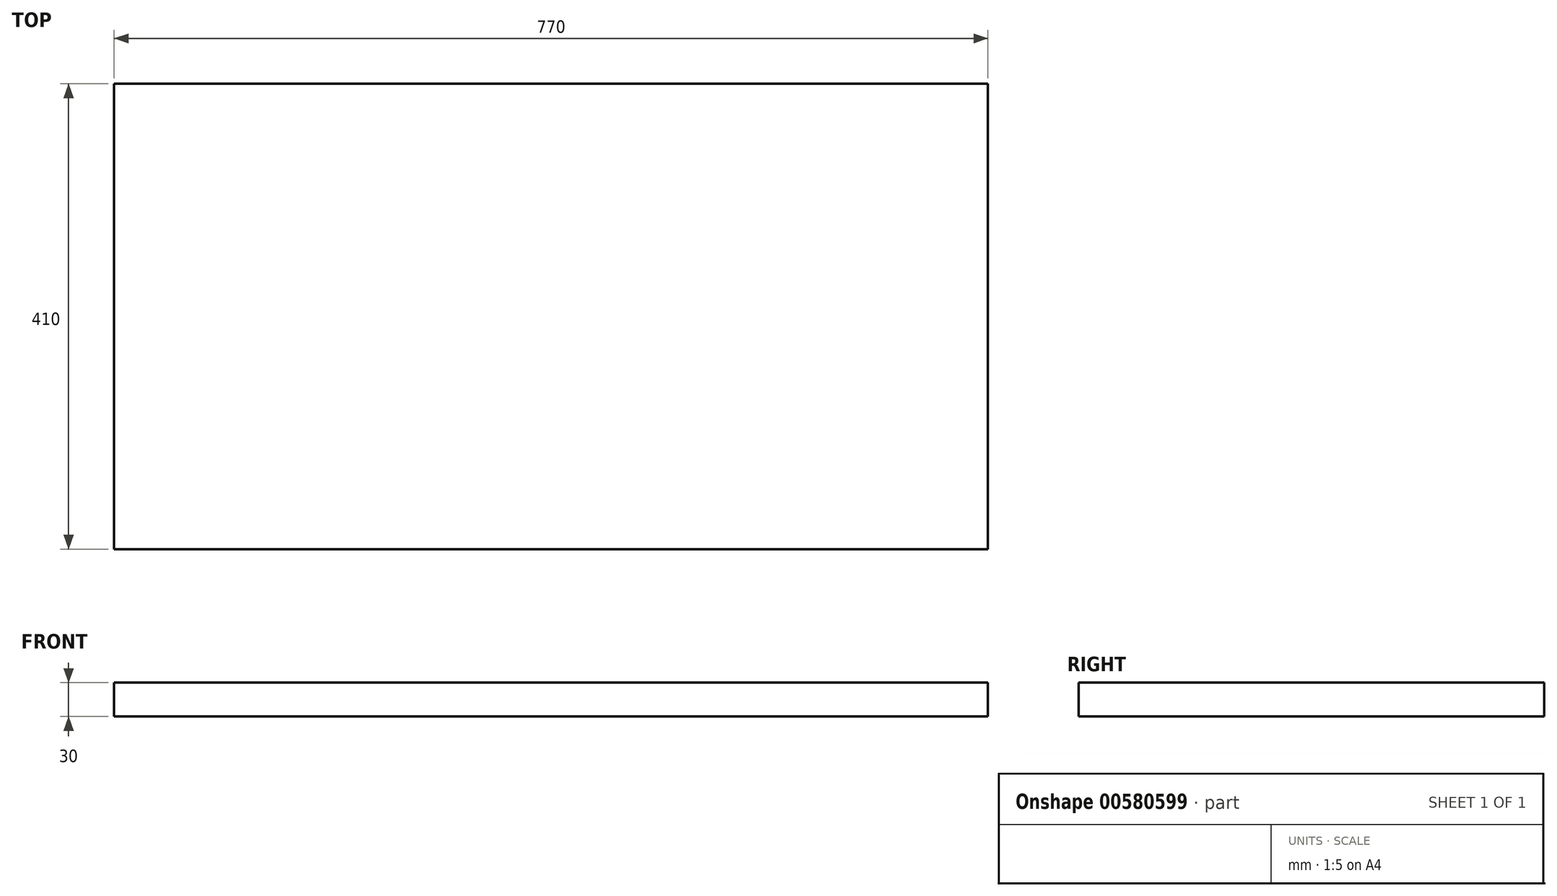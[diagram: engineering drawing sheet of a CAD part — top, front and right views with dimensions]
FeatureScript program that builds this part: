
annotation { "Feature Type Name" : "Feature", "Feature Type Description" : "" }
export const myFeature = defineFeature(function(context is Context, id is Id, definition is map)
    precondition{}
    {
        {
            var Q0;
            Q0=qCreatedBy(makeId("Top.planeOp"),FACE);
            var sketch = newSketch(context, id + "F0", { "sketchPlane" : qUnion([Q0])});
            skFitSpline(sketch, "E0", {"points": [v(0, 23.64) * mm, v(7.35, 24.1) * mm, v(20.44, 20.95) * mm, v(27.7, 15.75) * mm, v(39.9, 10.55) * mm, v(42.68, 9.83) * mm, v(45.82, 6.78) * mm, v(53.35, 1.76) * mm, v(55.77, -6.76) * mm, v(48.42, -21.1) * mm, v(34.34, -25.77) * mm, v(23.94, -26.85) * mm, v(14.7, -26.67) * mm, v(-6.73, -17.97) * mm, v(-18.48, -17.52) * mm, v(-30.68, -16.9) * mm, v(-37.94, -15.28) * mm, v(-41, -15.82) * mm, v(-49.6, -10.26) * mm, v(-55.7, -2) * mm, v(-55.22, 4.94) * mm, v(-53.55, 10.1) * mm, v(-48.07, 14.32) * mm, v(-35.86, 25.47) * mm, v(-31.51, 27.35) * mm, v(-25.83, 26.87) * mm, v(-16.6, 24.9) * mm, v(-3.5, 23.55) * mm, v(0, 23.64) * mm]});
            skSolve(sketch);
        }
        {
            var Q0;
            Q0=qCreatedBy(makeId("Top.planeOp"),FACE);
            var sketch = newSketch(context, id + "F1", { "sketchPlane" : qUnion([Q0])});
            skLineSegment(sketch, "E1.bottom", {"start": v(-385, 205) * mm, "end": v(385, 205) * mm});
            skLineSegment(sketch, "E1.top", {"start": v(-385, -205) * mm, "end": v(385, -205) * mm});
            skLineSegment(sketch, "E1.left", {"start": v(-385, 205) * mm, "end": v(-385, -205) * mm});
            skLineSegment(sketch, "E1.right", {"start": v(385, 205) * mm, "end": v(385, -205) * mm});
            skPoint(sketch, "E1.middle", {"position": v(0, 0) * mm});
            skSolve(sketch);
        }
        {
            var Q0;
            Q0 = qSketchRegion(id + "F1", true);
            extrude(context, id + "F2", {"entities" : qUnion([Q0]), "depth" : 30 * mm, "offsetDistance" : 25 * mm});
        }
    });
